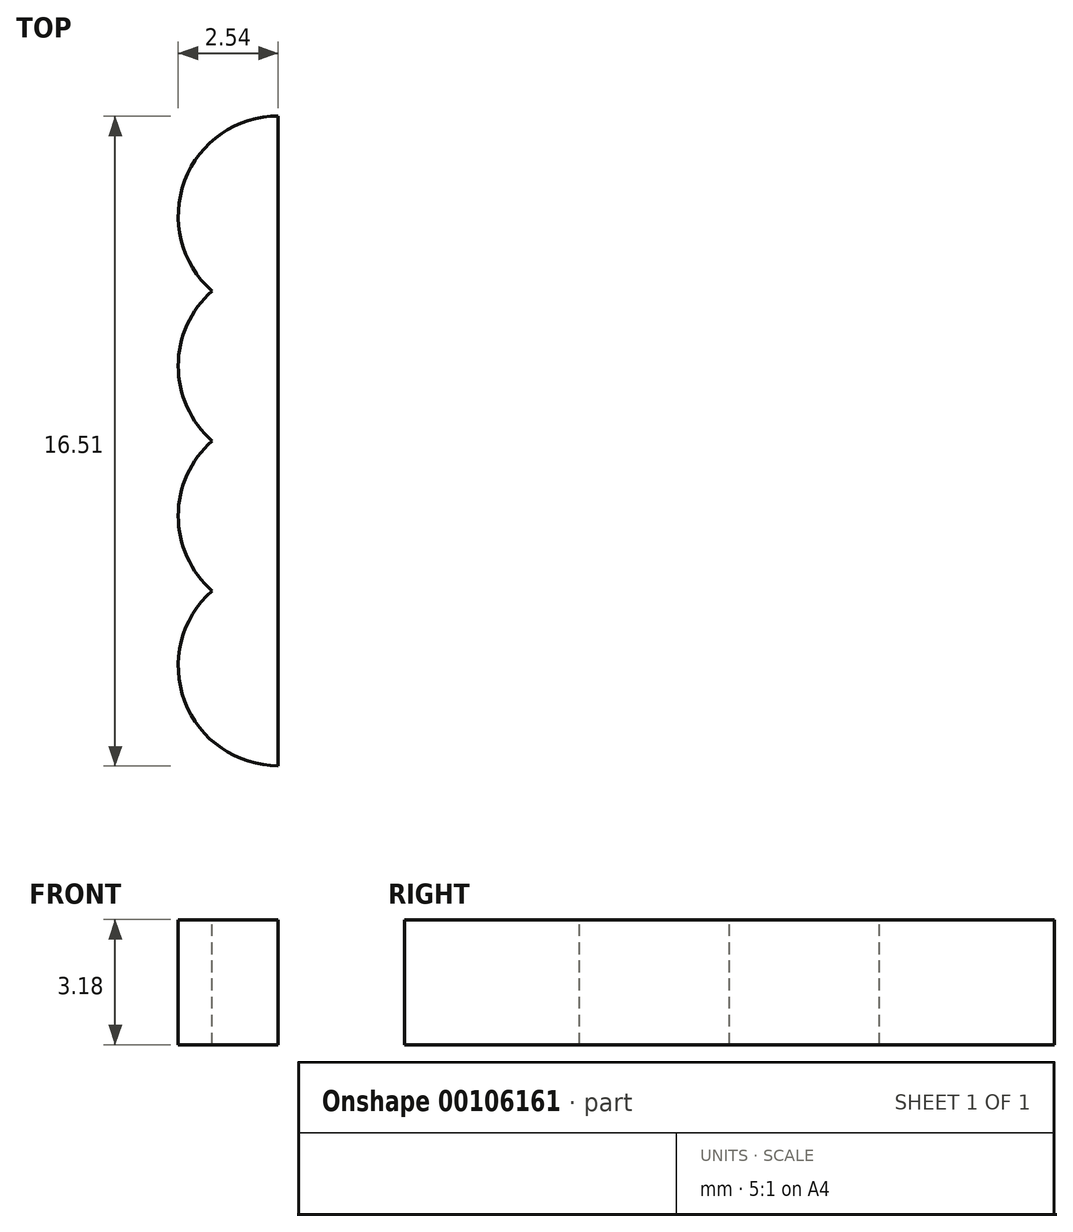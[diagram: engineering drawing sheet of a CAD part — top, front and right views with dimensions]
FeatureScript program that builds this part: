
annotation { "Feature Type Name" : "Feature", "Feature Type Description" : "" }
export const myFeature = defineFeature(function(context is Context, id is Id, definition is map)
    precondition{}
    {
        {
            var Q0;
            Q0=qCreatedBy(makeId("Top.planeOp"),FACE);
            var sketch = newSketch(context, id + "F0", { "sketchPlane" : qUnion([Q0])});
            skLineSegment(sketch, "E0.left", {"start": v(12.7, 47.4) * mm, "end": v(12.7, -47.4) * mm});
            skLineSegment(sketch, "E0.right", {"start": v(-12.7, 47.4) * mm, "end": v(-12.7, -47.4) * mm});
            skPoint(sketch, "E0.middle", {"position": v(0, 0) * mm});
            skLineSegment(sketch, "E1", {"start": v(0, -25.4) * mm, "end": v(0, 25.4) * mm});
            skArc(sketch, "E2", {"start": v(-12.7, -47.4) * mm, "mid": v(0, -50.8) * mm, "end": v(12.7, -47.4) * mm});
            skArc(sketch, "E3.trimOffspring", {"start": v(12.7, 47.4) * mm, "mid": v(0, 50.8) * mm, "end": v(-12.7, 47.4) * mm});
            skPoint(sketch, "E4", {"position": v(0, 50.8) * mm});
            skPoint(sketch, "E5", {"position": v(0, -50.8) * mm});
            skLineSegment(sketch, "E6", {"start": v(-12.7, 0) * mm, "end": v(12.7, 0) * mm});
            skSolve(sketch);
        }
        {
            var Q0;
            Q0=qSketchRegion(id+"F0",true);
            extrude(context, id + "F1", {"entities" : qUnion([Q0]), "depth" : 3.17 * mm});
        }
        {
            var Q0;
            Q0=makeQuery(id+"F1.opExtrude","CAP_FACE",FACE,{"disambiguationData":[OSD([sQuery(id+"F0.wireOp",EDGE,"E0.left"),sQuery(id+"F0.wireOp",EDGE,"E0.right"),sQuery(id+"F0.wireOp",EDGE,"E2"),sQuery(id+"F0.wireOp",EDGE,"E3.trimOffspring")])],"isStart":false});
            var sketch = newSketch(context, id + "F2", { "sketchPlane" : qUnion([Q0])});
            skLineSegment(sketch, "E7.bottom", {"start": v(7.94, 41.27) * mm, "end": v(-7.94, 41.27) * mm, "construction": true});
            skLineSegment(sketch, "E7.top", {"start": v(7.94, -34.93) * mm, "end": v(-7.94, -34.93) * mm, "construction": true});
            skLineSegment(sketch, "E7.left", {"start": v(7.94, 41.27) * mm, "end": v(7.94, -34.93) * mm, "construction": true});
            skLineSegment(sketch, "E7.right", {"start": v(-7.94, 41.27) * mm, "end": v(-7.94, -34.93) * mm, "construction": true});
            skPoint(sketch, "E7.middle", {"position": v(0, 3.18) * mm});
            skCircle(sketch, "E8", {"center": v(-7.94, 41.27) * mm, "radius": 2.38 * mm});
            skCircle(sketch, "E9", {"center": v(7.94, 41.27) * mm, "radius": 2.38 * mm});
            skCircle(sketch, "E10", {"center": v(-7.94, -34.93) * mm, "radius": 2.38 * mm});
            skCircle(sketch, "E11", {"center": v(7.94, -34.93) * mm, "radius": 2.38 * mm});
            skSolve(sketch);
        }
        {
            var Q0;
            Q0=qSketchRegion(id+"F2",true);
            extrude(context, id + "F3", {"entities" : qUnion([Q0]), "operationType" : NewBodyOperationType.REMOVE, "endBound" : BoundingType.UP_TO_NEXT, "oppositeDirection" : true, "depth" : 25.4 * mm});
        }
        {
            var Q0;
            Q0=makeQuery(id+"F1.opExtrude","CAP_FACE",FACE,{"disambiguationData":[OSD([sQuery(id+"F0.wireOp",EDGE,"E0.left"),sQuery(id+"F0.wireOp",EDGE,"E0.right"),sQuery(id+"F0.wireOp",EDGE,"E2"),sQuery(id+"F0.wireOp",EDGE,"E3.trimOffspring")])],"isStart":false});
            var sketch = newSketch(context, id + "F4", { "sketchPlane" : qUnion([Q0])});
            skCircle(sketch, "E12", {"center": v(0, 19.05) * mm, "radius": 7.62 * mm});
            skLineSegment(sketch, "E13", {"start": v(0, 0) * mm, "end": v(0, 19.05) * mm, "construction": true});
            skCircle(sketch, "E14", {"center": v(0, 44.45) * mm, "radius": 2.03 * mm});
            skLineSegment(sketch, "E15", {"start": v(-12.7, 19.05) * mm, "end": v(12.7, 19.05) * mm, "construction": true});
            skArc(sketch, "E16", {"start": v(-11.02, 22.86) * mm, "mid": v(-13.6, 27.14) * mm, "end": v(-12.7, 22.23) * mm});
            skArc(sketch, "E17", {"start": v(-11.02, 19.05) * mm, "mid": v(-10.16, 20.96) * mm, "end": v(-11.02, 22.86) * mm});
            skArc(sketch, "E18", {"start": v(-11.02, 15.24) * mm, "mid": v(-10.16, 17.14) * mm, "end": v(-11.02, 19.05) * mm});
            skArc(sketch, "E19", {"start": v(-12.7, 15.88) * mm, "mid": v(-13.6, 10.96) * mm, "end": v(-11.02, 15.24) * mm});
            skLineSegment(sketch, "E20", {"start": v(-12.7, 24.77) * mm, "end": v(-12.7, 20.96) * mm, "construction": true});
            skLineSegment(sketch, "E21", {"start": v(-12.7, 13.33) * mm, "end": v(-12.7, 17.14) * mm, "construction": true});
            skLineSegment(sketch, "E22", {"start": v(-12.7, 17.14) * mm, "end": v(-12.7, 20.96) * mm, "construction": true});
            skArc(sketch, "E23.MirrorC", {"start": v(14.38, 15.24) * mm, "mid": v(12.7, 10.8) * mm, "end": v(11.02, 15.24) * mm});
            skArc(sketch, "E24.MirrorC", {"start": v(14.38, 19.05) * mm, "mid": v(15.24, 17.14) * mm, "end": v(14.38, 15.24) * mm});
            skArc(sketch, "E25.MirrorC", {"start": v(14.38, 22.86) * mm, "mid": v(15.24, 20.96) * mm, "end": v(14.38, 19.05) * mm});
            skArc(sketch, "E26.MirrorC", {"start": v(11.02, 22.86) * mm, "mid": v(12.7, 27.3) * mm, "end": v(14.38, 22.86) * mm});
            skArc(sketch, "E27.trimOffspring", {"start": v(-12.7, 19.69) * mm, "mid": v(-15.24, 17.14) * mm, "end": v(-12.7, 14.6) * mm});
            skArc(sketch, "E28.trimOffspring", {"start": v(-12.7, 23.5) * mm, "mid": v(-15.24, 20.96) * mm, "end": v(-12.7, 18.41) * mm});
            skArc(sketch, "E29.trimOffspring", {"start": v(11.02, 19.05) * mm, "mid": v(10.16, 20.96) * mm, "end": v(11.02, 22.86) * mm});
            skArc(sketch, "E30.trimOffspring", {"start": v(11.02, 15.24) * mm, "mid": v(10.16, 17.14) * mm, "end": v(11.02, 19.05) * mm});
            skSolve(sketch);
        }
        {
            var Q0;
            {var subQ5=sQuery(id+"F4.wireOp",EDGE,"hyidi4E8-9G4u-DJ1j-ocSj-n68gthOh2VMQ.top");Q0=makeQuery(id+"F4.imprint","IMPRINT",FACE,{"disambiguationData":[TD([[makeQuery(id+"F4.imprint","IMPRINT",EDGE,{"derivedFrom":subQ5}),-1.0]])]});}
            var Q1;
            Q1=makeQuery(id+"F4.imprint","IMPRINT",FACE,{"disambiguationData":[TD([[makeQuery(id+"F4.imprint","IMPRINT",EDGE,{"derivedFrom":sQuery(id+"F4.wireOp",EDGE,"E12")}),1.0]])]});
            var Q2;
            {var subQ5=sQuery(id+"F4.wireOp",EDGE,"E17");Q2=makeQuery(id+"F4.imprint","IMPRINT",FACE,{"disambiguationData":[TD([[makeQuery(id+"F4.imprint","IMPRINT",EDGE,{"derivedFrom":subQ5}),1.0]])]});}
            var Q3;
            {var subQ1=sQuery(id+"F4.wireOp",EDGE,"E29.trimOffspring");Q3=makeQuery(id+"F4.imprint","IMPRINT",FACE,{"disambiguationData":[TD([[makeQuery(id+"F4.imprint","IMPRINT",EDGE,{"derivedFrom":subQ1}),-1.0]])]});}
            var Q4;
            Q4=makeQuery(id+"F4.imprint","IMPRINT",FACE,{"disambiguationData":[TD([[makeQuery(id+"F4.imprint","IMPRINT",EDGE,{"derivedFrom":sQuery(id+"F4.wireOp",EDGE,"E14")}),1.0]])]});
            extrude(context, id + "F5", {"entities" : qUnion([Q0, Q1, Q2, Q3, Q4]), "operationType" : NewBodyOperationType.REMOVE, "oppositeDirection" : true, "depth" : 25.4 * mm});
        }
    });
